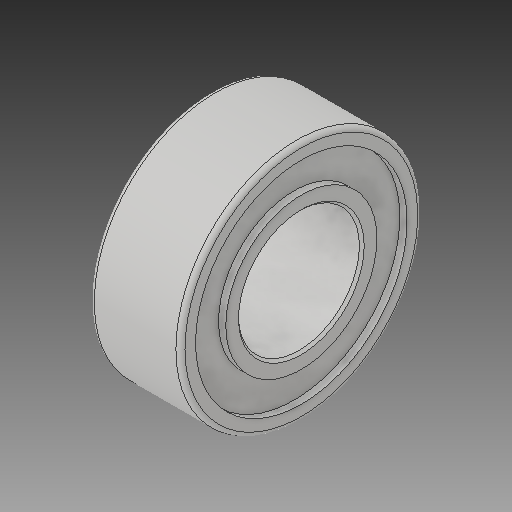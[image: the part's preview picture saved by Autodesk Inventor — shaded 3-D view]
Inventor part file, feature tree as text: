
AUTODESK INVENTOR PART (.ipt)
format: ipt  version: 2017 (Build 210142000, 142)  size: 184,832 bytes
history: native  units: in
note: dims shown in document units (in); Inventor stores cm internally (conversion verified against a paired STEP export)
features: chamfer x1
ambient origin geometry x8: Origin, YZ Plane, XZ Plane, XY Plane, X Axis, Y Axis, Z Axis, Center Point
bodies: Solid1 (feature_tree)
feature tree (1):
  chamfer  "Chamfer1"  [1 undecoded]
note: 1 required parameter value undecoded (feature->parameter linkage not recoverable at this tier; creation-order binding heuristic only, values carry confidence <= 0.55)
